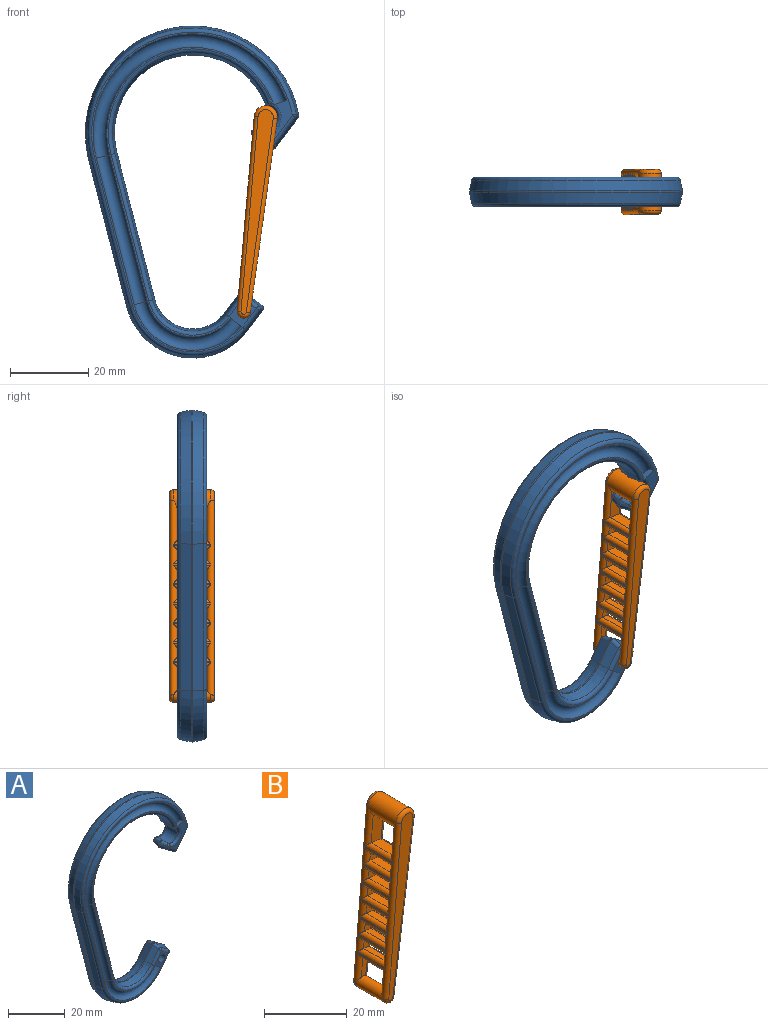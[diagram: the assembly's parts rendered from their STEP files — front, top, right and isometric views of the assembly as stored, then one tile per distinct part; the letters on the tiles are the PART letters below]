
ASSEMBLY  parts=2 mates=1
PART A: 111 faces, bbox 62.4x49.8x88.7 mm
  f0: plane 81.79x51.36mm, normal (0,1,0), area 153.5mm2, adj f26,f33,f34,f35,f36,f37,f39,f40
  f1: plane 81.79x51.36mm, normal (0,-1,0), area 153.5mm2, adj f26,f28,f29,f30,f31,f32,f38,f41
  f2: plane 2.76x0.97mm, normal (-0.78,-0.21,0.59), area 1.4mm2, adj f46,f57,f62,f107
  f3: cone r=20mm half-angle=12deg, axis (0,-1,0), area 172.5mm2, adj f14,f47,f58,f63
  f4: cone r=20mm half-angle=12deg, axis (0,1,0), area 172.5mm2, adj f15,f51,f59,f63
  f5: plane 4.36x3.39mm, normal (-0.59,-0.21,-0.78), area 13.7mm2, adj f42,f64,f82,f107
  f6: plane 7.76x5.83mm, normal (0.78,-0.21,-0.59), area 25.6mm2, adj f66,f82,f85,f89
  f7: cone r=27.5mm half-angle=12deg, axis (0,1,0), area 245.7mm2, adj f8,f68,f78,f89
  f8: plane 37.65x10.25mm, normal (-0.95,-0.21,-0.24), area 108.9mm2, adj f7,f9,f70,f79
  f9: cone r=17.5mm half-angle=12deg, axis (0,1,0), area 108.4mm2, adj f8,f10,f72,f80
  f10: plane 5.18x4.35mm, normal (0.78,-0.21,-0.59), area 17.4mm2, adj f9,f73,f81,f94
  f11: plane 4.36x3.39mm, normal (0.59,-0.21,0.78), area 13.7mm2, adj f71,f94,f97,f101
  f12: plane 5.53x4mm, normal (-0.78,-0.21,0.59), area 17.4mm2, adj f13,f38,f69,f101
  f13: cone r=10mm half-angle=12deg, axis (0,-1,0), area 65.3mm2, adj f12,f14,f41,f67
  f14: plane 37.65x10.25mm, normal (0.95,-0.21,0.24), area 108.9mm2, adj f3,f13,f45,f65
  f15: plane 37.65x10.25mm, normal (0.95,0.21,0.24), area 108.9mm2, adj f4,f16,f44,f65
  f16: cone r=10mm half-angle=12deg, axis (0,1,0), area 65.3mm2, adj f15,f17,f40,f67
  f17: plane 5.53x4mm, normal (-0.78,0.21,0.59), area 17.4mm2, adj f16,f39,f69,f105
  f18: plane 4.36x3.39mm, normal (0.59,0.21,0.78), area 13.7mm2, adj f71,f98,f102,f105
  f19: plane 5.18x4.35mm, normal (0.78,0.21,-0.59), area 17.4mm2, adj f20,f73,f77,f98
  f20: cone r=17.5mm half-angle=12deg, axis (0,-1,0), area 108.4mm2, adj f19,f21,f72,f76
  f21: plane 37.65x10.25mm, normal (-0.95,0.21,-0.24), area 108.9mm2, adj f20,f22,f70,f75
  f22: cone r=27.5mm half-angle=12deg, axis (0,-1,0), area 245.7mm2, adj f21,f68,f74,f93
  f23: plane 7.76x5.83mm, normal (0.78,0.21,-0.59), area 25.6mm2, adj f66,f86,f90,f93
  f24: plane 4.36x3.39mm, normal (-0.59,0.21,-0.78), area 13.7mm2, adj f43,f64,f86,f109
  f25: plane 2.76x0.97mm, normal (-0.78,0.21,0.59), area 1.4mm2, adj f49,f56,f62,f109
  f26: cylinder r=1.7mm len=7.5mm, axis (0,-1,0), area 80.1mm2, adj f0,f1
  f27: cylinder r=2.95mm len=5.84mm, axis (0,-1,0), area 54.4mm2, adj f48,f50,f56,f57,f58,f59
  f28: plane 2.8x2.1mm, normal (-0.6,0,-0.8), area 4.8mm2, adj f1,f30
  f29: plane 3.3x1.75mm, normal (-0.33,0,0.94), area 4.8mm2, adj f1,f32,f48
  f30: torus R=13.75mm, axis (0,1,0), area 169.7mm2, adj f1,f28,f31
  f31: cylinder r=1.75mm len=38.38mm, axis (-0.25,0,0.97), area 212.9mm2, adj f1,f30,f32
  f32: torus R=23.75mm, axis (0,1,0), area 399.2mm2, adj f1,f29,f31,f48
  f33: plane 2.8x2.1mm, normal (-0.6,0,-0.8), area 4.8mm2, adj f0,f35
  f34: plane 3.3x1.75mm, normal (-0.33,0,0.94), area 4.8mm2, adj f0,f37,f50
  f35: torus R=13.75mm, axis (0,-1,0), area 169.7mm2, adj f0,f33,f36
  f36: cylinder r=1.75mm len=38.38mm, axis (-0.25,0,0.97), area 212.9mm2, adj f0,f35,f37
  f37: torus R=23.75mm, axis (0,-1,0), area 399.2mm2, adj f0,f34,f36,f50
  f38: cylinder r=1mm len=5.3mm, axis (-0.6,0,-0.8), area 8mm2, adj f1,f12,f41,f99
  f39: cylinder r=1mm len=5.3mm, axis (0.6,0,0.8), area 8mm2, adj f0,f17,f40,f104
  f40: torus R=11.61mm, axis (0,-1,0), area 33.7mm2, adj f0,f16,f39,f44
  f41: torus R=11.61mm, axis (0,-1,0), area 33.7mm2, adj f1,f13,f38,f45
  f42: cylinder r=1mm len=4.02mm, axis (0.8,0,-0.6), area 5.8mm2, adj f1,f5,f83,f106
  f43: cylinder r=1mm len=4.02mm, axis (-0.8,0,0.6), area 5.8mm2, adj f0,f24,f88,f110
  f44: cylinder r=1mm len=37.74mm, axis (-0.25,0,0.97), area 52.7mm2, adj f0,f15,f40,f51
  f45: cylinder r=1mm len=37.74mm, axis (0.25,0,-0.97), area 52.7mm2, adj f1,f14,f41,f47
  f46: cylinder r=1mm len=0.93mm, axis (0.6,0,0.8), area 0.3mm2, adj f1,f2,f53,f106
  f47: torus R=21.61mm, axis (0,-1,0), area 86.7mm2, adj f1,f3,f45,f54
  f48: torus R=3.95mm, axis (0,-1,0), area 16.6mm2, adj f1,f27,f29,f32,f53,f54
  f49: cylinder r=1mm len=0.93mm, axis (-0.6,0,-0.8), area 0.3mm2, adj f0,f25,f52,f110
  f50: torus R=3.95mm, axis (0,-1,0), area 16.6mm2, adj f0,f27,f34,f37,f52,f55
  f51: torus R=21.61mm, axis (0,-1,0), area 86.7mm2, adj f0,f4,f44,f55
  f52: sphere r=1mm, area 1.3mm2, adj f49,f50,f56
  f53: sphere r=1mm, area 1.3mm2, adj f46,f48,f57
  f54: sphere r=1mm, area 0.8mm2, adj f47,f48,f58
  f55: sphere r=1mm, area 0.8mm2, adj f50,f51,f59
  f56: bspline ~2.96x1.72mm, area 4mm2, adj f25,f27,f52,f60
  f57: bspline ~2.96x1.72mm, area 4mm2, adj f2,f27,f53,f60
  f58: bspline ~5.03x1.7mm, area 2.6mm2, adj f3,f27,f54,f61
  f59: bspline ~5.03x1.7mm, area 2.6mm2, adj f4,f27,f55,f61
  f60: sphere r=1mm, area 0.4mm2, adj f56,f57,f62
  f61: sphere r=1mm, area 0.2mm2, adj f58,f59,f63
  f62: cylinder r=1mm len=0.61mm, axis (0.6,0,0.8), area 0.3mm2, adj f2,f25,f60,f108
  f63: torus R=21.02mm, axis (0,1,0), area 25.2mm2, adj f3,f4,f61,f65
  f64: cylinder r=1mm len=4.38mm, axis (0.8,0,-0.6), area 2.3mm2, adj f5,f24,f84,f108
  f65: cylinder r=1mm len=37.51mm, axis (0.25,0,-0.97), area 16.2mm2, adj f14,f15,f63,f67
  f66: cylinder r=1mm len=7.63mm, axis (0.6,0,0.8), area 4mm2, adj f6,f23,f84,f91
  f67: torus R=11.02mm, axis (0,1,0), area 9.4mm2, adj f13,f16,f65,f69
  f68: torus R=26.48mm, axis (0,1,0), area 37.1mm2, adj f7,f22,f70,f91
  f69: cylinder r=1mm len=5.2mm, axis (-0.6,0,-0.8), area 2.7mm2, adj f12,f17,f67,f103
  f70: cylinder r=1mm len=37.51mm, axis (0.25,0,-0.97), area 16.2mm2, adj f8,f21,f68,f72
  f71: cylinder r=1mm len=4.38mm, axis (0.8,0,-0.6), area 2.3mm2, adj f11,f18,f96,f103
  f72: torus R=16.48mm, axis (0,1,0), area 16.4mm2, adj f9,f20,f70,f73
  f73: cylinder r=1mm len=5.2mm, axis (-0.6,0,-0.8), area 2.7mm2, adj f10,f19,f72,f96
  f74: torus R=25.89mm, axis (0,-1,0), area 115.8mm2, adj f0,f22,f75,f92
  f75: cylinder r=1mm len=37.74mm, axis (-0.25,0,0.97), area 52.7mm2, adj f0,f21,f74,f76
  f76: torus R=15.89mm, axis (0,-1,0), area 50.4mm2, adj f0,f20,f75,f77
  f77: cylinder r=1mm len=5.3mm, axis (0.6,0,0.8), area 8mm2, adj f0,f19,f76,f100
  f78: torus R=25.89mm, axis (0,-1,0), area 115.8mm2, adj f1,f7,f79,f87
  f79: cylinder r=1mm len=37.74mm, axis (0.25,0,-0.97), area 52.7mm2, adj f1,f8,f78,f80
  f80: torus R=15.89mm, axis (0,-1,0), area 50.4mm2, adj f1,f9,f79,f81
  f81: cylinder r=1mm len=5.3mm, axis (-0.6,0,-0.8), area 8mm2, adj f1,f10,f80,f95
  f82: cylinder r=1mm len=2.83mm, axis (0.04,0.96,-0.28), area 4.4mm2, adj f5,f6,f83,f84
  f83: sphere r=1mm, area 1.2mm2, adj f42,f82,f85
  f84: sphere r=1mm, area 0.8mm2, adj f64,f66,f82,f86
  f85: cylinder r=1mm len=7.53mm, axis (0.6,0,0.8), area 11.8mm2, adj f1,f6,f83,f87
  f86: cylinder r=1mm len=2.83mm, axis (-0.04,0.96,0.28), area 4.4mm2, adj f23,f24,f84,f88
  f87: sphere r=1mm, area 0.6mm2, adj f78,f85,f89
  f88: sphere r=1mm, area 1.2mm2, adj f43,f86,f90
  f89: bspline ~37.43x8.59mm, area 2.3mm2, adj f6,f7,f87,f91
  f90: cylinder r=1mm len=7.53mm, axis (-0.6,0,-0.8), area 11.8mm2, adj f0,f23,f88,f92
  f91: sphere r=1mm, area 0.4mm2, adj f66,f68,f89,f93
  f92: sphere r=1mm, area 0.6mm2, adj f74,f90,f93
  f93: bspline ~37.43x8.59mm, area 2.3mm2, adj f22,f23,f91,f92
  f94: cylinder r=1mm len=2.83mm, axis (0.28,0.96,0.04), area 4.4mm2, adj f10,f11,f95,f96
  f95: sphere r=1mm, area 1.2mm2, adj f81,f94,f97
  f96: sphere r=1mm, area 0.8mm2, adj f71,f73,f94,f98
  f97: cylinder r=1mm len=4.02mm, axis (0.8,0,-0.6), area 5.8mm2, adj f1,f11,f95,f99
  f98: cylinder r=1mm len=2.83mm, axis (-0.28,0.96,-0.04), area 4.4mm2, adj f18,f19,f96,f100
  f99: sphere r=1mm, area 1.2mm2, adj f38,f97,f101
  f100: sphere r=1mm, area 1.2mm2, adj f77,f98,f102
  f101: cylinder r=1mm len=2.83mm, axis (-0.04,0.96,0.28), area 4.4mm2, adj f11,f12,f99,f103
  f102: cylinder r=1mm len=4.02mm, axis (-0.8,0,0.6), area 5.8mm2, adj f0,f18,f100,f104
  f103: sphere r=1mm, area 0.8mm2, adj f69,f71,f101,f105
  f104: sphere r=1mm, area 1.2mm2, adj f39,f102,f105
  f105: cylinder r=1mm len=2.83mm, axis (0.04,0.96,-0.28), area 4.4mm2, adj f17,f18,f103,f104
  f106: sphere r=1mm, area 1.1mm2, adj f42,f46,f107
  f107: cylinder r=1mm len=2.83mm, axis (-0.28,0.96,-0.04), area 4.4mm2, adj f2,f5,f106,f108
  f108: sphere r=1mm, area 0.8mm2, adj f62,f64,f107,f109
  f109: cylinder r=1mm len=2.83mm, axis (0.28,0.96,0.04), area 4.4mm2, adj f24,f25,f108,f110
  f110: sphere r=1mm, area 1.1mm2, adj f43,f49,f109
PART B: 84 faces, bbox 10.5x11.5x54.6 mm
  f0: plane 9.5x0.5mm, normal (0.99,0,-0.14), area 4.8mm2, adj f64,f79,f82,f83
  f1: plane 9.5x0.5mm, normal (0.99,0,-0.14), area 4.7mm2, adj f64,f77,f78,f82
  f2: plane 9.5x0.5mm, normal (0.99,0,-0.14), area 4.7mm2, adj f64,f75,f76,f82
  f3: plane 9.5x0.5mm, normal (0.99,0,-0.14), area 4.8mm2, adj f64,f73,f74,f82
  f4: plane 9.5x0.5mm, normal (0.99,0,-0.14), area 4.7mm2, adj f64,f71,f72,f82
  f5: plane 9.5x0.5mm, normal (0.99,0,-0.14), area 4.7mm2, adj f64,f69,f70,f82
  f6: plane 9.5x0.5mm, normal (-1,0,0.09), area 4.8mm2, adj f48,f61,f62,f63
  f7: plane 9.5x0.5mm, normal (-1,0,0.09), area 4.8mm2, adj f48,f59,f60,f63
  f8: plane 9.5x0.5mm, normal (-1,0,0.09), area 4.8mm2, adj f48,f57,f58,f63
  f9: plane 9.5x0.5mm, normal (-1,0,0.09), area 4.8mm2, adj f48,f55,f56,f63
  f10: plane 9.5x0.5mm, normal (-1,0,0.09), area 4.8mm2, adj f48,f53,f54,f63
  f11: plane 9.5x0.5mm, normal (-1,0,0.09), area 4.8mm2, adj f48,f51,f52,f63
  f12: plane 7.5x3.04mm, normal (-0.14,0,-0.99), area 23mm2, adj f29,f44,f48,f52,f63,f77
  f13: plane 7.5x3.06mm, normal (0.14,0,0.99), area 23.2mm2, adj f31,f46,f51,f78
  f14: plane 7.5x2.79mm, normal (-0.14,0,-0.99), area 21.1mm2, adj f28,f43,f48,f54,f63,f75
  f15: plane 7.5x2.81mm, normal (0.14,0,0.99), area 21.3mm2, adj f29,f44,f53,f76
  f16: plane 7.5x2.54mm, normal (-0.14,0,-0.99), area 19.2mm2, adj f27,f42,f48,f56,f63,f73
  f17: plane 7.5x2.56mm, normal (0.14,0,0.99), area 19.4mm2, adj f28,f43,f55,f74
  f18: plane 7.5x2.29mm, normal (-0.14,0,-0.99), area 17.3mm2, adj f26,f41,f48,f58,f63,f71
  f19: plane 7.5x2.32mm, normal (0.14,0,0.99), area 17.5mm2, adj f27,f42,f57,f72
  f20: plane 7.5x2.04mm, normal (-0.14,0,-0.99), area 15.5mm2, adj f25,f40,f48,f60,f63,f69
  f21: plane 7.5x2.07mm, normal (0.14,0,0.99), area 15.7mm2, adj f26,f41,f59,f70
  f22: plane 7.5x1.79mm, normal (-0.14,0,-0.99), area 13.6mm2, adj f24,f39,f48,f62,f63,f67
  f23: plane 7.5x1.82mm, normal (0.14,0,0.99), area 13.8mm2, adj f25,f40,f61,f68
  f24: plane 5.81x2.24mm, normal (0,1,0), area 9mm2, adj f22,f32,f48,f64
  f25: plane 2.75x2.21mm, normal (0,1,0), area 4.9mm2, adj f20,f23,f48,f61,f64
  f26: plane 2.79x2.46mm, normal (0,1,0), area 5.5mm2, adj f18,f21,f48,f59,f64
  f27: plane 2.82x2.71mm, normal (0,1,0), area 6.1mm2, adj f16,f19,f48,f57,f64
  f28: plane 2.96x2.86mm, normal (0,1,0), area 6.8mm2, adj f14,f17,f48,f55,f64
  f29: plane 3.21x2.89mm, normal (0,1,0), area 7.4mm2, adj f12,f15,f48,f53,f64
  f30: plane 8.43x4.47mm, normal (0,1,0), area 27.1mm2, adj f35,f38,f48,f49,f64
  f31: plane 3.46x2.93mm, normal (0,1,0), area 8mm2, adj f13,f37,f48,f51,f64
  f32: cylinder r=1.7mm len=9.5mm, axis (0,1,0), area 93.6mm2, adj f24,f39,f48,f63,f64,f65,f81,f82
  f33: plane 9.5x0.5mm, normal (-1,0,0.09), area 4.8mm2, adj f48,f49,f50,f63
  f34: plane 9.5x0.5mm, normal (0.99,0,-0.14), area 4.8mm2, adj f64,f67,f68,f82
  f35: cylinder r=2.95mm len=9.5mm, axis (0,1,0), area 161.8mm2, adj f30,f45,f48,f63,f64,f66,f80,f82
  f36: plane 52.32x8.29mm, normal (0,-1,0), area 139.4mm2, adj f48,f64,f65,f66
  f37: plane 7.5x3.28mm, normal (-0.14,0,-0.99), area 24.9mm2, adj f31,f46,f48,f50,f63,f79
  f38: plane 7.5x3.31mm, normal (0.14,0,0.99), area 25.1mm2, adj f30,f45,f49,f83
  f39: plane 5.81x2.24mm, normal (0,-1,0), area 9mm2, adj f22,f32,f63,f82
  f40: plane 2.75x2.21mm, normal (0,-1,0), area 4.9mm2, adj f20,f23,f61,f63,f82
  f41: plane 2.79x2.46mm, normal (0,-1,0), area 5.5mm2, adj f18,f21,f59,f63,f82
  f42: plane 2.82x2.71mm, normal (0,-1,0), area 6.1mm2, adj f16,f19,f57,f63,f82
  f43: plane 2.96x2.86mm, normal (0,-1,0), area 6.8mm2, adj f14,f17,f55,f63,f82
  f44: plane 3.21x2.89mm, normal (0,-1,0), area 7.4mm2, adj f12,f15,f53,f63,f82
  f45: plane 8.43x4.47mm, normal (0,-1,0), area 27.1mm2, adj f35,f38,f49,f63,f82
  f46: plane 3.46x2.93mm, normal (0,-1,0), area 8mm2, adj f13,f37,f51,f63,f82
  f47: plane 52.32x8.29mm, normal (0,1,0), area 139.4mm2, adj f63,f80,f81,f82
  f48: cylinder r=1mm len=49.86mm, axis (-0.09,0,-1), area 134.1mm2, adj f6,f7,f8,f9,f10,f11,f12,f14
  f49: cylinder r=1mm len=9.5mm, axis (0,-1,0), area 13.3mm2, adj f30,f33,f38,f45,f48,f63
  f50: cylinder r=1mm len=9.5mm, axis (0,1,0), area 12.5mm2, adj f33,f37,f48,f63
  f51: cylinder r=1mm len=9.5mm, axis (0,-1,0), area 13.3mm2, adj f11,f13,f31,f46,f48,f63
  f52: cylinder r=1mm len=9.5mm, axis (0,1,0), area 12.5mm2, adj f11,f12,f48,f63
  f53: cylinder r=1mm len=9.5mm, axis (0,-1,0), area 13.3mm2, adj f10,f15,f29,f44,f48,f63
  f54: cylinder r=1mm len=9.5mm, axis (0,1,0), area 12.5mm2, adj f10,f14,f48,f63
  f55: cylinder r=1mm len=9.5mm, axis (0,-1,0), area 13.3mm2, adj f9,f17,f28,f43,f48,f63
  f56: cylinder r=1mm len=9.5mm, axis (0,1,0), area 12.5mm2, adj f9,f16,f48,f63
  f57: cylinder r=1mm len=9.5mm, axis (0,-1,0), area 13.3mm2, adj f8,f19,f27,f42,f48,f63
  f58: cylinder r=1mm len=9.5mm, axis (0,1,0), area 12.5mm2, adj f8,f18,f48,f63
  f59: cylinder r=1mm len=9.5mm, axis (0,-1,0), area 13.3mm2, adj f7,f21,f26,f41,f48,f63
  f60: cylinder r=1mm len=9.5mm, axis (0,1,0), area 12.5mm2, adj f7,f20,f48,f63
  f61: cylinder r=1mm len=9.5mm, axis (0,-1,0), area 13.3mm2, adj f6,f23,f25,f40,f48,f63
  f62: cylinder r=1mm len=9.5mm, axis (0,1,0), area 12.5mm2, adj f6,f22,f48,f63
  f63: cylinder r=1mm len=49.86mm, axis (-0.09,0,-1), area 134.1mm2, adj f6,f7,f8,f9,f10,f11,f12,f14
  f64: cylinder r=1mm len=49.63mm, axis (0.14,0,0.99), area 134.2mm2, adj f0,f1,f2,f3,f4,f5,f24,f25
  f65: torus R=0.7mm, axis (0,-1,0), area 6.5mm2, adj f32,f36,f48,f64
  f66: torus R=1.95mm, axis (0,-1,0), area 13mm2, adj f35,f36,f48,f64
  f67: cylinder r=1mm len=9.5mm, axis (0,-1,0), area 12.9mm2, adj f22,f34,f64,f82
  f68: cylinder r=1mm len=9.5mm, axis (0,1,0), area 12.9mm2, adj f23,f34,f64,f82
  f69: cylinder r=1mm len=9.5mm, axis (0,-1,0), area 12.9mm2, adj f5,f20,f64,f82
  f70: cylinder r=1mm len=9.5mm, axis (0,1,0), area 12.9mm2, adj f5,f21,f64,f82
  f71: cylinder r=1mm len=9.5mm, axis (0,-1,0), area 12.9mm2, adj f4,f18,f64,f82
  f72: cylinder r=1mm len=9.5mm, axis (0,1,0), area 12.9mm2, adj f4,f19,f64,f82
  f73: cylinder r=1mm len=9.5mm, axis (0,-1,0), area 12.9mm2, adj f3,f16,f64,f82
  f74: cylinder r=1mm len=9.5mm, axis (0,1,0), area 12.9mm2, adj f3,f17,f64,f82
  f75: cylinder r=1mm len=9.5mm, axis (0,-1,0), area 12.9mm2, adj f2,f14,f64,f82
  f76: cylinder r=1mm len=9.5mm, axis (0,1,0), area 12.9mm2, adj f2,f15,f64,f82
  f77: cylinder r=1mm len=9.5mm, axis (0,-1,0), area 12.9mm2, adj f1,f12,f64,f82
  f78: cylinder r=1mm len=9.5mm, axis (0,1,0), area 12.9mm2, adj f1,f13,f64,f82
  f79: cylinder r=1mm len=9.5mm, axis (0,-1,0), area 12.9mm2, adj f0,f37,f64,f82
  f80: torus R=1.95mm, axis (0,1,0), area 13mm2, adj f35,f47,f63,f82
  f81: torus R=0.7mm, axis (0,1,0), area 6.5mm2, adj f32,f47,f63,f82
  f82: cylinder r=1mm len=49.63mm, axis (0.14,0,0.99), area 134.2mm2, adj f0,f1,f2,f3,f4,f5,f32,f34
  f83: cylinder r=1mm len=9.5mm, axis (0,1,0), area 12.9mm2, adj f0,f38,f64,f82
PLACE A at identity fixed
PLACE B at identity
MATE revolute B.f32 <-> A.f26  axis (0,1,0) through (13.01,0,-5.57)mm
